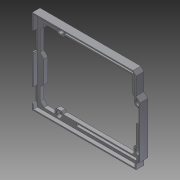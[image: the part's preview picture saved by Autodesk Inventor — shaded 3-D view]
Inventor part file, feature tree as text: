
AUTODESK INVENTOR PART (.ipt)
format: ipt  version: 2012 SP1 (Build 160190100, 190)  size: 305,152 bytes
history: native  units: in
note: dims shown in document units (in); Inventor stores cm internally (conversion verified against a paired STEP export)
features: extrude x5, sketch x5, chamfer x3, projected_geometry x1
ambient origin geometry x8: Origin, YZ Plane, XZ Plane, XY Plane, X Axis, Y Axis, Z Axis, Center Point
feature tree (14):
  extrude  "Extrusion2"  Depth=2.1in
  extrude  "Extrusion3"  Depth=2.04in
  extrude  "Extrusion4"  Depth=1.59in
  extrude  "Extrusion5"  Depth=2.6in
  extrude  "Extrusion7"  Depth=0.2in
  chamfer  "Chamfer3"  Distance=0.008in
  chamfer  "Chamfer5"  Distance=0.1in
  chamfer  "Chamfer6"  Distance=0.029in
  sketch  "Sketch1"  dims[d0=2.54in d1=2.1in]
  sketch  "Sketch2"  dims[d4=2.6in d5=2.04in]
  sketch  "Sketch4"  dims[d6=2.7in d7=1.59in]
  sketch  "Sketch5"  dims[d8=1.49in d9=2.6in]
  projected_geometry  "Projected Loop1"
  sketch  "Sketch7"  dims[d10=0.1in d11=0.2in d15=0.008in d16=0.1in d17=0.0in d18=0.029in d19=2.54in d20=2.1in d21=2.6in d22=2.04in d23=2.7in d24=1.59in d25=1.49in d26=2.6in d27=0.1in d28=0.2in d29=0.008in d30=0.029in d31=0.2in d32=0.1in d33=0.0in d35=0.49in d36=0.1125in d37=1.26in d38=1.74in d39=0.09in d40=0.0in d41=0.0625in d42=1.0in d43=2.55in d44=0.7in d45=2.55in d46=0.0625in d47=2.0312in d48=0.0688in d49=0.085in d50=0.0in d51=0.0in d52=0.475in d54=0.45in d56=1.198in d57=2.505in d58=0.2in d61=0.1in d66=0.1in d67=0.1in d68=0.1in d69=0.1in d70=0.55in d71=0.1in d72=0.125in d73=2.0in d74=0.125in d75=0.6in d76=2.6in d77=1.4in d78=0.125in d79=0.125in d80=2.6in d81=0.3in d97=0.1in d101=0.1in d102=0.1in d106=0.0625in d107=1.0in d108=2.55in d109=0.7in d110=2.55in d111=0.0625in d112=2.0312in d113=0.0688in d114=0.0in d115=0.475in d116=0.45in d117=0.1in d118=0.1in d119=0.1in d120=0.1in d121=0.1in d122=0.1in d123=0.1in d124=1.0in d125=0.0in d126=0.1in d127=0.125in d128=45.0deg d132=0.1in d133=0.125in d134=45.0deg d135=0.1in d136=0.05in d137=0.1125in d138=0.05in d139=0.015in d140=0.125in d141=45.0deg]
